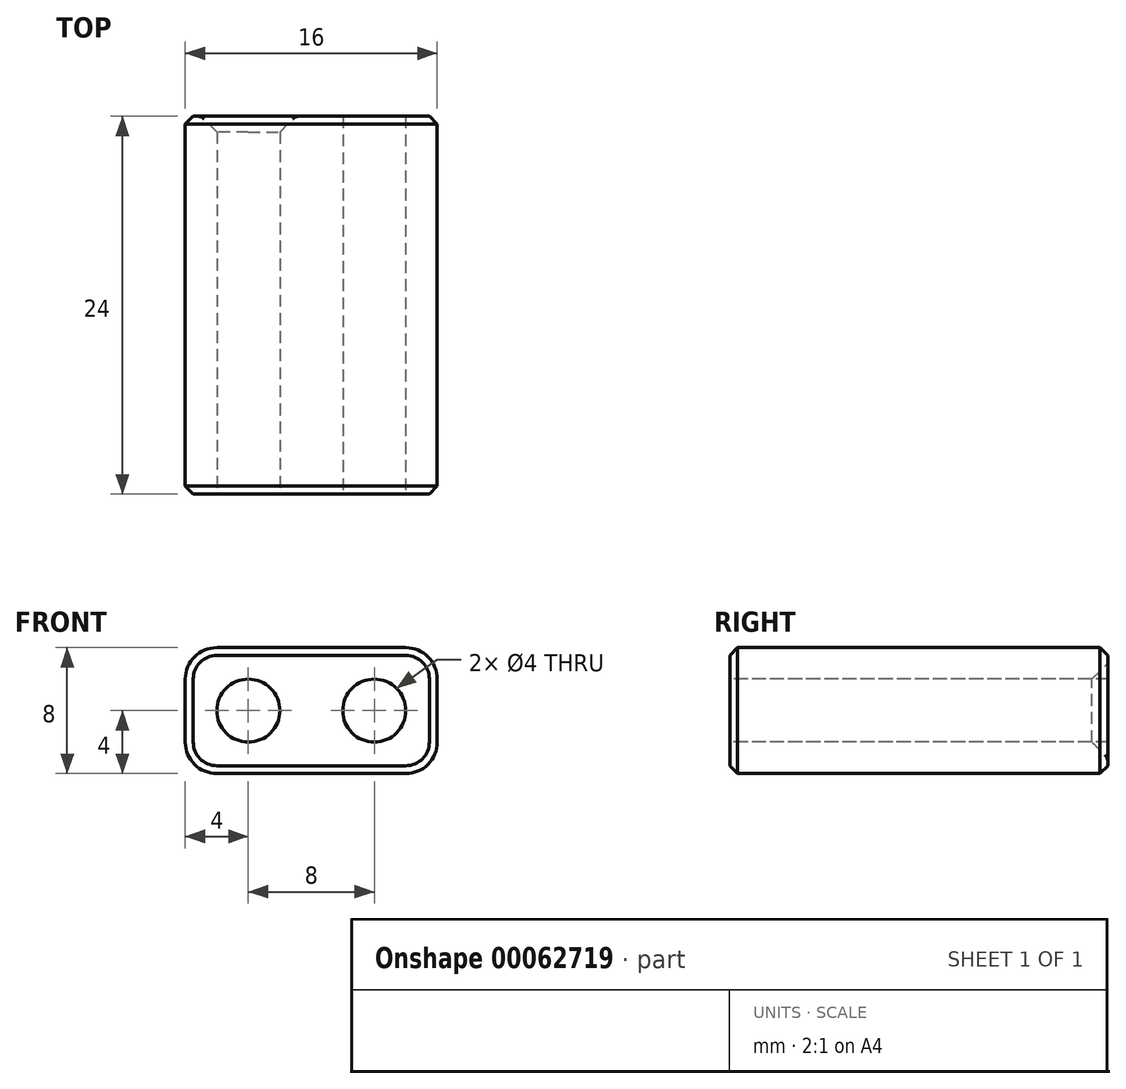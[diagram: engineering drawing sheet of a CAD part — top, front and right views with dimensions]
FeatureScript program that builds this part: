
annotation { "Feature Type Name" : "Feature", "Feature Type Description" : "" }
export const myFeature = defineFeature(function(context is Context, id is Id, definition is map)
    precondition{}
    {
        {
            var Q0;
            Q0=qCreatedBy(makeId("Top.planeOp"),FACE);
            var sketch = newSketch(context, id + "F0", { "sketchPlane" : qUnion([Q0])});
            skLineSegment(sketch, "E0.bottom", {"start": v(-8, 12) * mm, "end": v(8, 12) * mm});
            skLineSegment(sketch, "E0.top", {"start": v(-8, -12) * mm, "end": v(8, -12) * mm});
            skLineSegment(sketch, "E0.left", {"start": v(-8, 12) * mm, "end": v(-8, -12) * mm});
            skLineSegment(sketch, "E0.right", {"start": v(8, 12) * mm, "end": v(8, -12) * mm});
            skLineSegment(sketch, "E1", {"start": v(-8, 0) * mm, "end": v(8, 0) * mm, "construction": true});
            skSolve(sketch);
        }
        {
            var Q0;
            Q0=makeQuery(id+"F0.imprint","IMPRINT",FACE,{"disambiguationData":[TD([[makeQuery(id+"F0.imprint","IMPRINT",EDGE,{"derivedFrom":sQuery(id+"F0.wireOp",EDGE,"E0.bottom")}),-1.0]])]});
            var Q1;
            Q1 = qSketchRegion(id + "F0", true);
            extrude(context, id + "F1", {"entities" : qUnion([Q0, Q1]), "depth" : 8 * mm});
        }
        {
            var Q0;
            Q0=makeQuery(id+"F1.opExtrude","SWEPT_FACE",FACE,{"disambiguationData":[OSD([sQuery(id+"F0.wireOp",EDGE,"E0.top")])]});
            var sketch = newSketch(context, id + "F2", { "sketchPlane" : qUnion([Q0])});
            skCircle(sketch, "E2", {"center": v(-4, 4) * mm, "radius": 2 * mm});
            skSolve(sketch);
        }
        {
            var Q0;
            Q0 = qSketchRegion(id + "F2", true);
            extrude(context, id + "F3", {"entities" : qUnion([Q0]), "operationType" : NewBodyOperationType.REMOVE, "oppositeDirection" : true, "depth" : 50 * mm});
        }
        {
            var Q0;
            Q0=makeQuery(id+"F1.opExtrude","SWEPT_BODY",BODY,{"disambiguationData":[OSD([sQuery(id+"F0.wireOp",EDGE,"E0.bottom"),sQuery(id+"F0.wireOp",EDGE,"E0.top"),sQuery(id+"F0.wireOp",EDGE,"E0.left"),sQuery(id+"F0.wireOp",EDGE,"E0.right")])]});
            var Q1;
            Q1=qCreatedBy(makeId("Right.planeOp"),FACE);
            mirror(context, id + "F4", {"operationType" : NewBodyOperationType.INTERSECT, "entities" : qUnion([Q0]), "mirrorPlane" : qUnion([Q1])});
        }
        {
            var Q0;
            Q0=makeQuery(id+"F1.opExtrude","CAP_EDGE",EDGE,{"disambiguationData":[OSD([sQuery(id+"F0.wireOp",EDGE,"E0.left")])],"isStart":false});
            var Q1;
            Q1=makeQuery(id+"F1.opExtrude","CAP_EDGE",EDGE,{"disambiguationData":[OSD([sQuery(id+"F0.wireOp",EDGE,"E0.right")])],"isStart":false});
            var Q2;
            Q2=makeQuery(id+"F1.opExtrude","CAP_EDGE",EDGE,{"disambiguationData":[OSD([sQuery(id+"F0.wireOp",EDGE,"E0.right")])],"isStart":true});
            var Q3;
            Q3=makeQuery(id+"F1.opExtrude","CAP_EDGE",EDGE,{"disambiguationData":[OSD([sQuery(id+"F0.wireOp",EDGE,"E0.left")])],"isStart":true});
            fillet(context, id + "F5", {"entities" : qUnion([Q0, Q1, Q2, Q3]), "radius" : 2 * mm, "tangentPropagation" : true, "allowEdgeOverflow" : false});
        }
        {
            var Q0;
            Q0=makeQuery(id+"F1.opExtrude","CAP_EDGE",EDGE,{"disambiguationData":[OSD([sQuery(id+"F0.wireOp",EDGE,"E0.top")])],"isStart":false});
            var Q1;
            Q1=makeQuery(id+"F1.opExtrude","CAP_EDGE",EDGE,{"disambiguationData":[OSD([sQuery(id+"F0.wireOp",EDGE,"E0.bottom")])],"isStart":false});
            chamfer(context, id + "F6", {"entities" : qUnion([Q0, Q1]), "width" : 0.5 * mm, "tangentPropagation" : true});
        }
        {
            var Q0;
            Q0=makeQuery(id+"F4.boolean.opBoolean","COPY",EDGE,{"derivedFrom":makeQuery(id+"F4.boolean.toolComplement.opBoolean","COPY",EDGE,{"derivedFrom":makeQuery(id+"F4.opPattern","COPY",EDGE,{"derivedFrom":makeQuery(id+"F3.boolean.opBoolean","INTERSECT",EDGE,{"derivedFrom":[makeQuery(id+"F1.opExtrude","SWEPT_FACE",FACE,{"disambiguationData":[OSD([sQuery(id+"F0.wireOp",EDGE,"E0.bottom")])]}),makeQuery(id+"F3.opExtrude","SWEPT_FACE",FACE,{"disambiguationData":[OSD([sQuery(id+"F2.wireOp",EDGE,"E2")])]})]}),"instanceName":"1"})})});
            var Q1;
            Q1=makeQuery(id+"F3.boolean.opBoolean","INTERSECT",EDGE,{"derivedFrom":[makeQuery(id+"F1.opExtrude","SWEPT_FACE",FACE,{"disambiguationData":[OSD([sQuery(id+"F0.wireOp",EDGE,"E0.bottom")])]}),makeQuery(id+"F3.opExtrude","SWEPT_FACE",FACE,{"disambiguationData":[OSD([sQuery(id+"F2.wireOp",EDGE,"E2")])]})]});
            chamfer(context, id + "F7", {"entities" : qUnion([Q0, Q1]), "width" : 1 * mm, "tangentPropagation" : true});
        }
        {
            var Q0;
            {var subQ0=makeQuery(id+"F1.opExtrude","SWEPT_FACE",FACE,{"disambiguationData":[OSD([sQuery(id+"F0.wireOp",EDGE,"E0.bottom")])]});Q0=makeQuery(id+"F7.opChamfer","BLEND_EDGE",EDGE,{"blendedFrom":[makeQuery(id+"F4.boolean.opBoolean","COPY",EDGE,{"derivedFrom":makeQuery(id+"F4.boolean.toolComplement.opBoolean","COPY",EDGE,{"derivedFrom":makeQuery(id+"F4.opPattern","COPY",EDGE,{"derivedFrom":makeQuery(id+"F3.boolean.opBoolean","INTERSECT",EDGE,{"derivedFrom":[subQ0,makeQuery(id+"F3.opExtrude","SWEPT_FACE",FACE,{"disambiguationData":[OSD([sQuery(id+"F2.wireOp",EDGE,"E2")])]})]}),"instanceName":"1"})})}),subQ0],"blendedInto":[subQ0]});}
            var Q1;
            {var subQ0=makeQuery(id+"F1.opExtrude","SWEPT_FACE",FACE,{"disambiguationData":[OSD([sQuery(id+"F0.wireOp",EDGE,"E0.bottom")])]});Q1=makeQuery(id+"F7.opChamfer","BLEND_EDGE",EDGE,{"blendedFrom":[makeQuery(id+"F3.boolean.opBoolean","INTERSECT",EDGE,{"derivedFrom":[subQ0,makeQuery(id+"F3.opExtrude","SWEPT_FACE",FACE,{"disambiguationData":[OSD([sQuery(id+"F2.wireOp",EDGE,"E2")])]})]}),subQ0],"blendedInto":[subQ0]});}
            fillet(context, id + "F8", {"entities" : qUnion([Q0, Q1]), "radius" : 0.5 * mm, "tangentPropagation" : true, "allowEdgeOverflow" : false});
        }
    });
